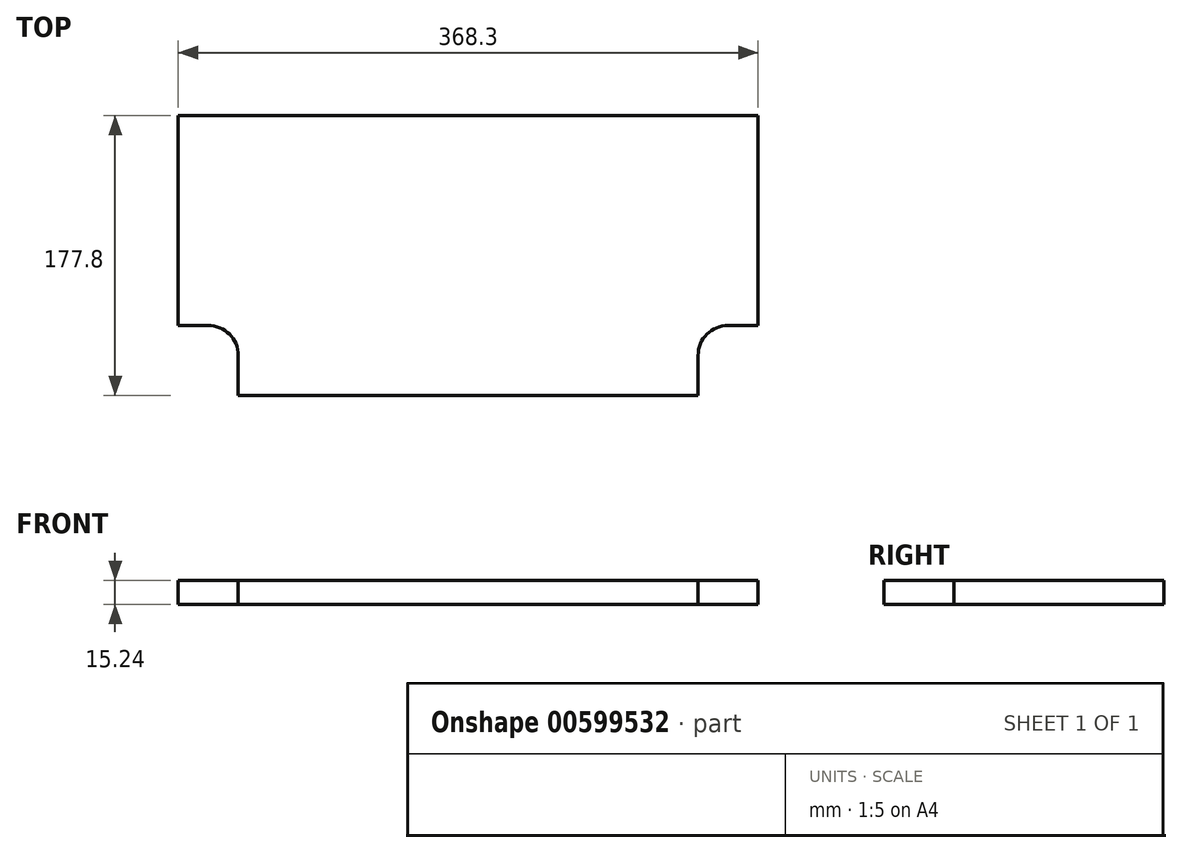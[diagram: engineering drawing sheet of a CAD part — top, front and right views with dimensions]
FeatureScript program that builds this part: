
annotation { "Feature Type Name" : "Feature", "Feature Type Description" : "" }
export const myFeature = defineFeature(function(context is Context, id is Id, definition is map)
    precondition{}
    {
        {
            var Q0;
            Q0=qCreatedBy(makeId("Top.planeOp"),FACE);
            var sketch = newSketch(context, id + "F0", { "sketchPlane" : qUnion([Q0])});
            skLineSegment(sketch, "E0.bottom", {"start": v(-184.15, 88.9) * mm, "end": v(184.15, 88.9) * mm});
            skLineSegment(sketch, "E0.top", {"start": v(-184.15, -88.9) * mm, "end": v(184.15, -88.9) * mm});
            skLineSegment(sketch, "E0.left", {"start": v(-184.15, 88.9) * mm, "end": v(-184.15, -88.9) * mm});
            skLineSegment(sketch, "E0.right", {"start": v(184.15, 88.9) * mm, "end": v(184.15, -88.9) * mm});
            skCircle(sketch, "E1", {"center": v(-165.1, -63.5) * mm, "radius": 19.05 * mm});
            skLineSegment(sketch, "E2", {"start": v(0, 88.9) * mm, "end": v(0, -88.9) * mm});
            skLineSegment(sketch, "E3", {"start": v(-146.05, -63.5) * mm, "end": v(-146.05, -88.9) * mm});
            skLineSegment(sketch, "E4", {"start": v(-184.15, 0) * mm, "end": v(184.15, 0) * mm});
            skCircle(sketch, "E5.MirrorC", {"center": v(165.1, -63.5) * mm, "radius": 19.05 * mm});
            skLineSegment(sketch, "E6.MirrorCS", {"start": v(146.05, -63.5) * mm, "end": v(146.05, -88.9) * mm});
            skLineSegment(sketch, "E7", {"start": v(-184.15, -44.45) * mm, "end": v(-165.1, -44.45) * mm});
            skLineSegment(sketch, "E8.MirrorCS", {"start": v(184.15, -44.45) * mm, "end": v(165.1, -44.45) * mm});
            skSolve(sketch);
        }
        {
            var Q0;
            Q0=makeQuery(id+"F0.imprint","IMPRINT",FACE,{"disambiguationData":[TD([[makeQuery(id+"F0.imprint","IMPRINT",EDGE,{"derivedFrom":sQuery(id+"F0.wireOp",EDGE,"E0.bottom")}),-1.0]])]});
            var Q1;
            {var subQ5=sQuery(id+"F0.wireOp",EDGE,"E3");Q1=makeQuery(id+"F0.imprint","IMPRINT",FACE,{"disambiguationData":[TD([[makeQuery(id+"F0.imprint","IMPRINT",EDGE,{"derivedFrom":subQ5}),1.0]])]});}
            var Q2;
            {var subQ7=sQuery(id+"F0.wireOp",EDGE,"E6.MirrorCS");Q2=makeQuery(id+"F0.imprint","IMPRINT",FACE,{"disambiguationData":[TD([[makeQuery(id+"F0.imprint","IMPRINT",EDGE,{"derivedFrom":subQ7}),-1.0]])]});}
            extrude(context, id + "F1", {"entities" : qUnion([Q0, Q1, Q2]), "depth" : 15.24 * mm, "offsetDistance" : 25.4 * mm});
        }
    });
